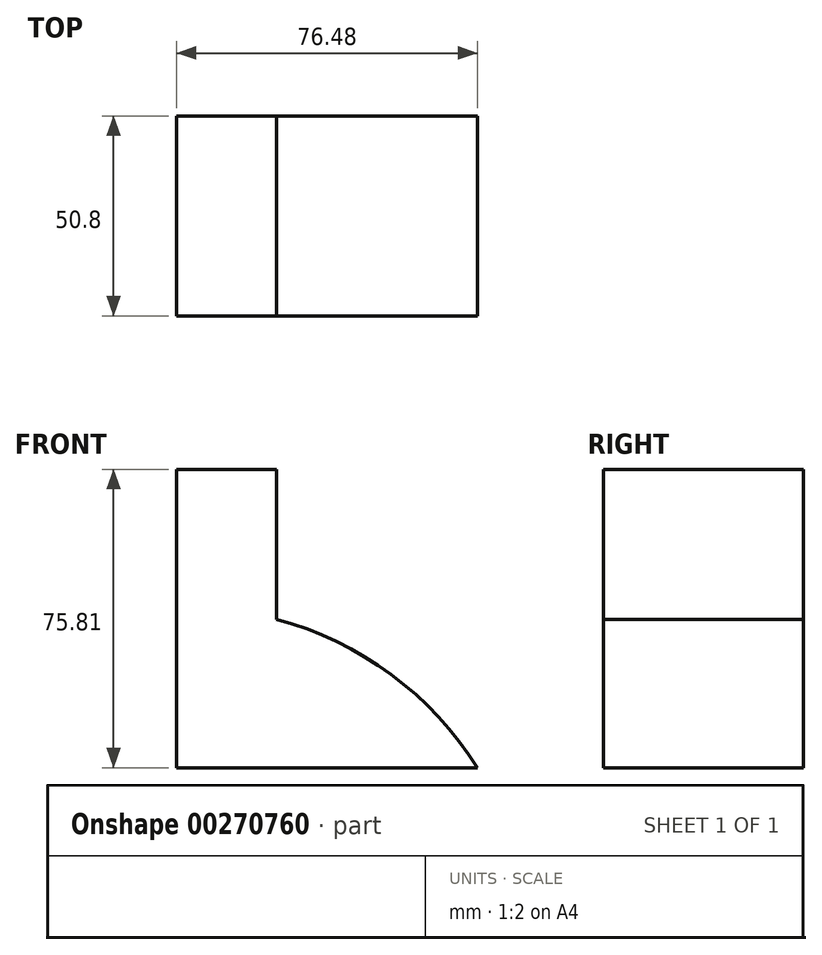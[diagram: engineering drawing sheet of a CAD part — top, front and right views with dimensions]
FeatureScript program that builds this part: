
annotation { "Feature Type Name" : "Feature", "Feature Type Description" : "" }
export const myFeature = defineFeature(function(context is Context, id is Id, definition is map)
    precondition{}
    {
        {
            var Q0;
            Q0=qCreatedBy(makeId("Front.planeOp"),FACE);
            var sketch = newSketch(context, id + "F0", { "sketchPlane" : qUnion([Q0])});
            skLineSegment(sketch, "E0", {"start": v(0, 0) * mm, "end": v(-76.48, 0) * mm});
            skLineSegment(sketch, "E1", {"start": v(-76.48, 0) * mm, "end": v(-76.48, 75.8) * mm});
            skLineSegment(sketch, "E2", {"start": v(-76.48, 75.8) * mm, "end": v(-51.08, 75.8) * mm});
            skLineSegment(sketch, "E3", {"start": v(-51.08, 75.8) * mm, "end": v(-51.08, 37.7) * mm});
            skArc(sketch, "E4", {"start": v(0, 0) * mm, "mid": v(-21.98, 23.67) * mm, "end": v(-51.08, 37.7) * mm});
            skSolve(sketch);
        }
        {
            var Q0;
            Q0 = qSketchRegion(id + "F0", true);
            extrude(context, id + "F1", {"entities" : qUnion([Q0]), "depth" : 50.8 * mm});
        }
    });
